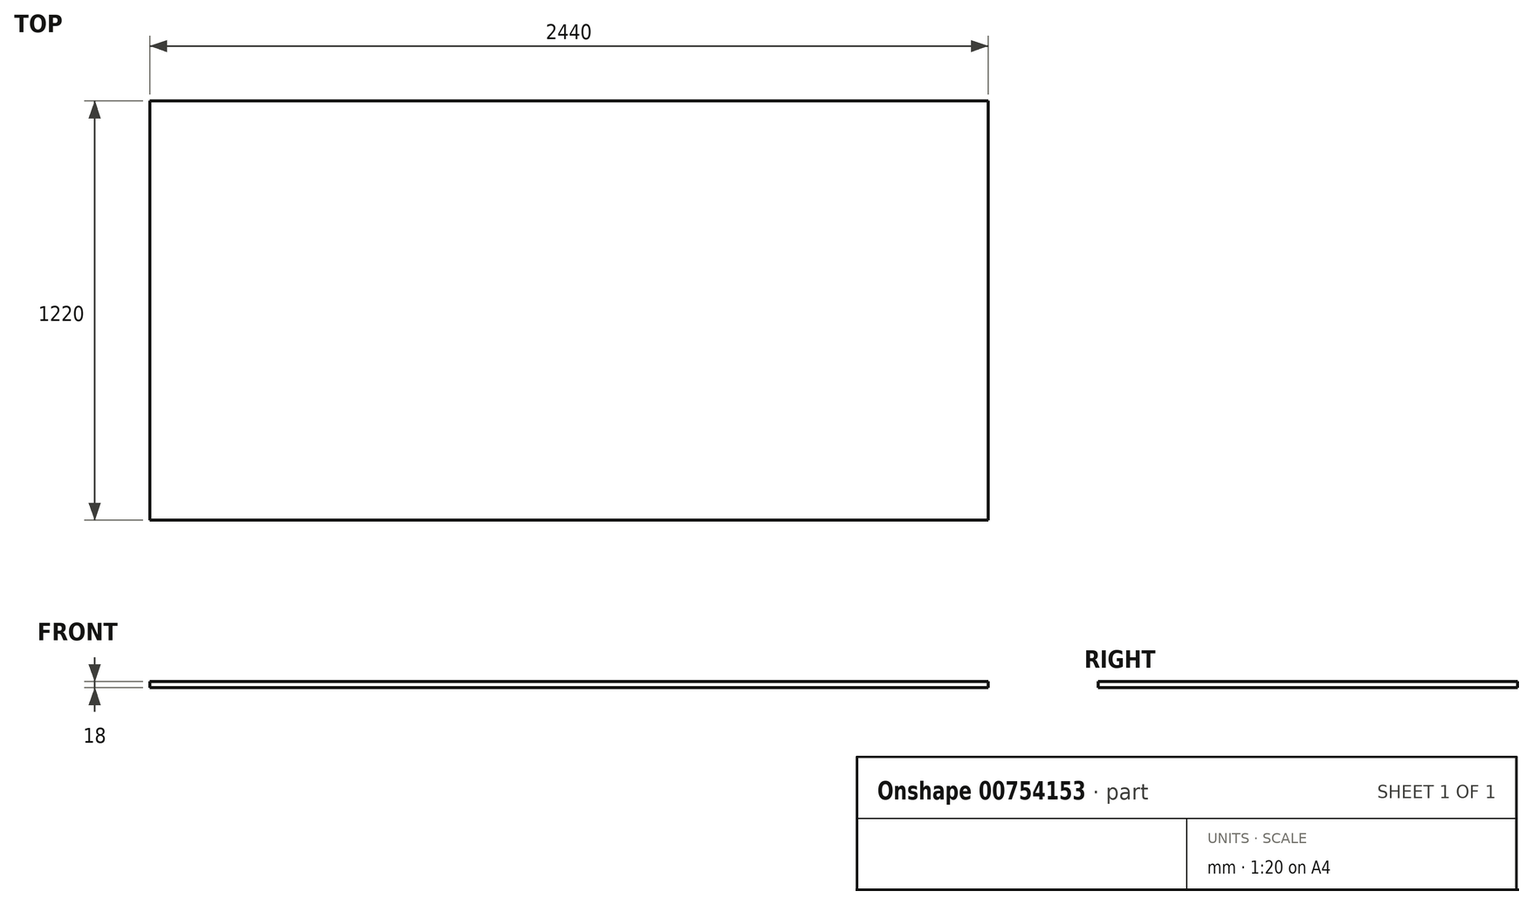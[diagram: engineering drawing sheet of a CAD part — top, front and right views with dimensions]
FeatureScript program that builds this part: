
annotation { "Feature Type Name" : "Feature", "Feature Type Description" : "" }
export const myFeature = defineFeature(function(context is Context, id is Id, definition is map)
    precondition{}
    {
        {
            var Q0;
            Q0=qCreatedBy(makeId("Top.planeOp"),FACE);
            var sketch = newSketch(context, id + "F0", { "sketchPlane" : qUnion([Q0])});
            skLineSegment(sketch, "E0.bottom", {"start": v(0, 0) * mm, "end": v(2440, 0) * mm});
            skLineSegment(sketch, "E0.top", {"start": v(0, 1220) * mm, "end": v(2440, 1220) * mm});
            skLineSegment(sketch, "E0.left", {"start": v(0, 0) * mm, "end": v(0, 1220) * mm});
            skLineSegment(sketch, "E0.right", {"start": v(2440, 0) * mm, "end": v(2440, 1220) * mm});
            skSolve(sketch);
        }
        {
            var Q0;
            Q0 = qSketchRegion(id + "F0", true);
            extrude(context, id + "F1", {"entities" : qUnion([Q0]), "depth" : 18 * mm, "offsetDistance" : 25 * mm});
        }
    });
